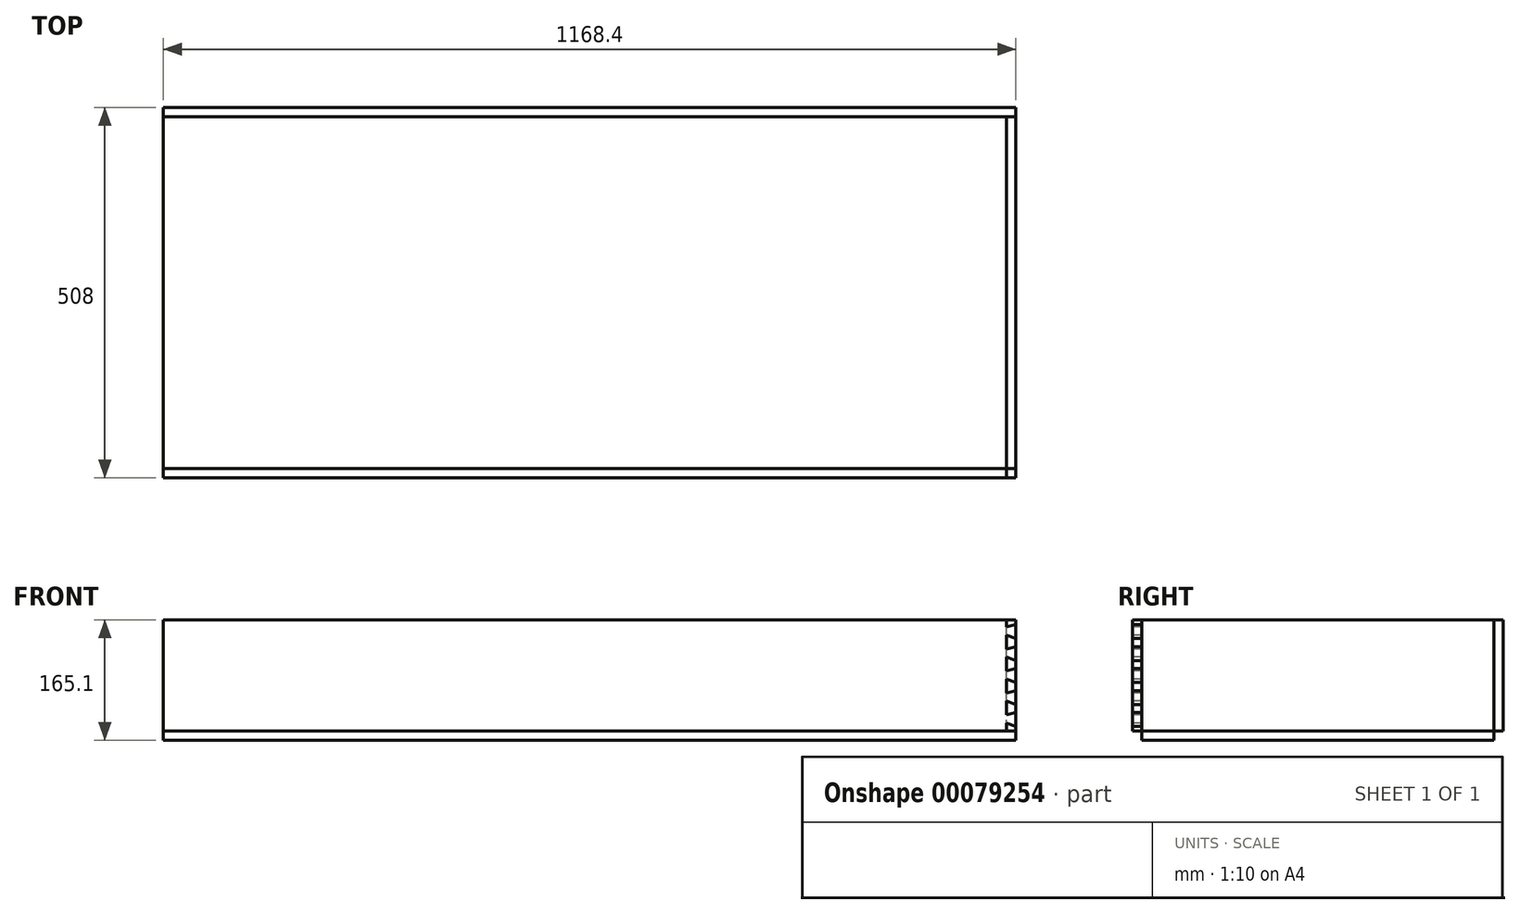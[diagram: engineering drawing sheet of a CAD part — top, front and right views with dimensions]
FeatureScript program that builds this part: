
annotation { "Feature Type Name" : "Feature", "Feature Type Description" : "" }
export const myFeature = defineFeature(function(context is Context, id is Id, definition is map)
    precondition{}
    {
        {
            var Q0;
            Q0=qCreatedBy(makeId("Top.planeOp"),FACE);
            var sketch = newSketch(context, id + "F0", { "sketchPlane" : qUnion([Q0])});
            skLineSegment(sketch, "E0.bottom", {"start": v(-589.95, 113.63) * mm, "end": v(578.45, 113.63) * mm});
            skLineSegment(sketch, "E0.top", {"start": v(-589.95, -368.97) * mm, "end": v(578.45, -368.97) * mm});
            skLineSegment(sketch, "E0.left", {"start": v(-589.95, 113.63) * mm, "end": v(-589.95, -368.97) * mm});
            skLineSegment(sketch, "E0.right", {"start": v(578.45, 113.63) * mm, "end": v(578.45, -368.97) * mm});
            skSolve(sketch);
        }
        {
            var Q0;
            Q0 = qSketchRegion(id + "F0", true);
            extrude(context, id + "F1", {"entities" : qUnion([Q0]), "endBound" : BoundingType.SYMMETRIC, "depth" : 12.7 * mm});
        }
        {
            var Q0;
            Q0=makeQuery(id+"F1.opExtrude","SWEPT_FACE",FACE,{"disambiguationData":[OSD([sQuery(id+"F0.wireOp",EDGE,"E0.top")])]});
            var sketch = newSketch(context, id + "F2", { "sketchPlane" : qUnion([Q0])});
            skPoint(sketch, "E1.oppositeSnap0", {"position": v(578.45, 0) * mm});
            skLineSegment(sketch, "E1.bottom", {"start": v(-589.95, 6.35) * mm, "end": v(578.45, 6.35) * mm});
            skLineSegment(sketch, "E1.top", {"start": v(-589.95, 158.75) * mm, "end": v(578.45, 158.75) * mm});
            skLineSegment(sketch, "E1.left", {"start": v(-589.95, 6.35) * mm, "end": v(-589.95, 158.75) * mm});
            skLineSegment(sketch, "E1.right", {"start": v(578.45, 6.35) * mm, "end": v(578.45, 158.75) * mm});
            skSolve(sketch);
        }
        {
            var Q0;
            Q0 = qSketchRegion(id + "F2", true);
            extrude(context, id + "F3", {"entities" : qUnion([Q0]), "depth" : 12.7 * mm});
        }
        {
            var Q0;
            Q0=makeQuery(id+"F1.opExtrude","SWEPT_FACE",FACE,{"disambiguationData":[OSD([sQuery(id+"F0.wireOp",EDGE,"E0.bottom")])]});
            var sketch = newSketch(context, id + "F4", { "sketchPlane" : qUnion([Q0])});
            skLineSegment(sketch, "E2.bottom", {"start": v(-578.45, 6.35) * mm, "end": v(589.95, 6.35) * mm});
            skLineSegment(sketch, "E2.top", {"start": v(-578.45, 158.75) * mm, "end": v(589.95, 158.75) * mm});
            skLineSegment(sketch, "E2.left", {"start": v(-578.45, 6.35) * mm, "end": v(-578.45, 158.75) * mm});
            skLineSegment(sketch, "E2.right", {"start": v(589.95, 6.35) * mm, "end": v(589.95, 158.75) * mm});
            skSolve(sketch);
        }
        {
            var Q0;
            Q0 = qSketchRegion(id + "F4", true);
            extrude(context, id + "F5", {"entities" : qUnion([Q0]), "depth" : 12.7 * mm});
        }
        {
            var Q0;
            Q0=makeQuery(id+"F1.opExtrude","SWEPT_FACE",FACE,{"disambiguationData":[OSD([sQuery(id+"F0.wireOp",EDGE,"E0.right")])]});
            var sketch = newSketch(context, id + "F6", { "sketchPlane" : qUnion([Q0])});
            skLineSegment(sketch, "E3.bottom", {"start": v(-368.97, 6.35) * mm, "end": v(113.63, 6.35) * mm});
            skLineSegment(sketch, "E3.top", {"start": v(-368.97, 158.75) * mm, "end": v(113.63, 158.75) * mm});
            skLineSegment(sketch, "E3.left", {"start": v(-368.97, 6.35) * mm, "end": v(-368.97, 158.75) * mm});
            skLineSegment(sketch, "E3.right", {"start": v(113.63, 6.35) * mm, "end": v(113.63, 158.75) * mm});
            skSolve(sketch);
        }
        {
            var Q0;
            Q0 = qSketchRegion(id + "F6", true);
            extrude(context, id + "F7", {"entities" : qUnion([Q0]), "oppositeDirection" : true, "depth" : 12.7 * mm});
        }
        {
            var Q0;
            Q0=makeQuery(id+"F3.opExtrude","CAP_FACE",FACE,{"disambiguationData":[OSD([sQuery(id+"F2.wireOp",EDGE,"E1.bottom"),sQuery(id+"F2.wireOp",EDGE,"E1.top"),sQuery(id+"F2.wireOp",EDGE,"E1.left"),sQuery(id+"F2.wireOp",EDGE,"E1.right")])],"isStart":false});
            var sketch = newSketch(context, id + "F8", { "sketchPlane" : qUnion([Q0])});
            skLineSegment(sketch, "E4", {"start": v(565.75, 158.75) * mm, "end": v(565.75, 11.9) * mm, "construction": true});
            skLineSegment(sketch, "E5", {"start": v(565.75, 149.23) * mm, "end": v(578.45, 152.4) * mm});
            skLineSegment(sketch, "E6", {"start": v(578.45, 133.35) * mm, "end": v(565.75, 138.11) * mm});
            skLineSegment(sketch, "E7", {"start": v(565.75, 119.06) * mm, "end": v(578.45, 122.24) * mm});
            skLineSegment(sketch, "E8", {"start": v(578.45, 103.19) * mm, "end": v(565.75, 107.95) * mm});
            skLineSegment(sketch, "E9", {"start": v(565.75, 88.9) * mm, "end": v(578.45, 92.08) * mm});
            skLineSegment(sketch, "E10", {"start": v(578.45, 73.03) * mm, "end": v(565.75, 77.79) * mm});
            skLineSegment(sketch, "E11", {"start": v(565.75, 58.74) * mm, "end": v(578.45, 61.91) * mm});
            skLineSegment(sketch, "E12", {"start": v(578.45, 42.86) * mm, "end": v(565.75, 47.63) * mm});
            skLineSegment(sketch, "E13", {"start": v(565.75, 17.45) * mm, "end": v(578.45, 12.7) * mm});
            skLineSegment(sketch, "E14", {"start": v(578.45, 31.75) * mm, "end": v(565.75, 28.58) * mm});
            skLineSegment(sketch, "E15", {"start": v(565.75, 158.75) * mm, "end": v(578.45, 158.75) * mm});
            skLineSegment(sketch, "E16", {"start": v(578.45, 158.75) * mm, "end": v(578.45, 152.4) * mm});
            skLineSegment(sketch, "E17", {"start": v(578.45, 133.35) * mm, "end": v(578.45, 122.24) * mm});
            skLineSegment(sketch, "E18", {"start": v(565.75, 119.06) * mm, "end": v(565.75, 138.11) * mm});
            skLineSegment(sketch, "E19", {"start": v(565.75, 107.95) * mm, "end": v(565.75, 88.9) * mm});
            skLineSegment(sketch, "E20", {"start": v(578.45, 92.08) * mm, "end": v(578.45, 103.19) * mm});
            skLineSegment(sketch, "E21", {"start": v(565.75, 77.79) * mm, "end": v(565.75, 58.74) * mm});
            skLineSegment(sketch, "E22", {"start": v(578.45, 61.91) * mm, "end": v(578.45, 73.03) * mm});
            skLineSegment(sketch, "E23", {"start": v(565.75, 47.63) * mm, "end": v(565.75, 28.58) * mm});
            skLineSegment(sketch, "E24", {"start": v(578.45, 31.75) * mm, "end": v(578.45, 42.86) * mm});
            skLineSegment(sketch, "E25", {"start": v(565.75, 17.45) * mm, "end": v(565.75, 6.35) * mm});
            skLineSegment(sketch, "E26", {"start": v(565.75, 6.35) * mm, "end": v(578.45, 6.35) * mm});
            skLineSegment(sketch, "E27", {"start": v(578.45, 6.35) * mm, "end": v(578.45, 12.7) * mm});
            skLineSegment(sketch, "E28", {"start": v(565.75, 158.75) * mm, "end": v(565.75, 149.23) * mm});
            skSolve(sketch);
        }
        {
            var Q0;
            Q0 = qSketchRegion(id + "F8", true);
            extrude(context, id + "F9", {"entities" : qUnion([Q0]), "operationType" : NewBodyOperationType.REMOVE, "oppositeDirection" : true, "depth" : 12.7 * mm});
        }
    });
